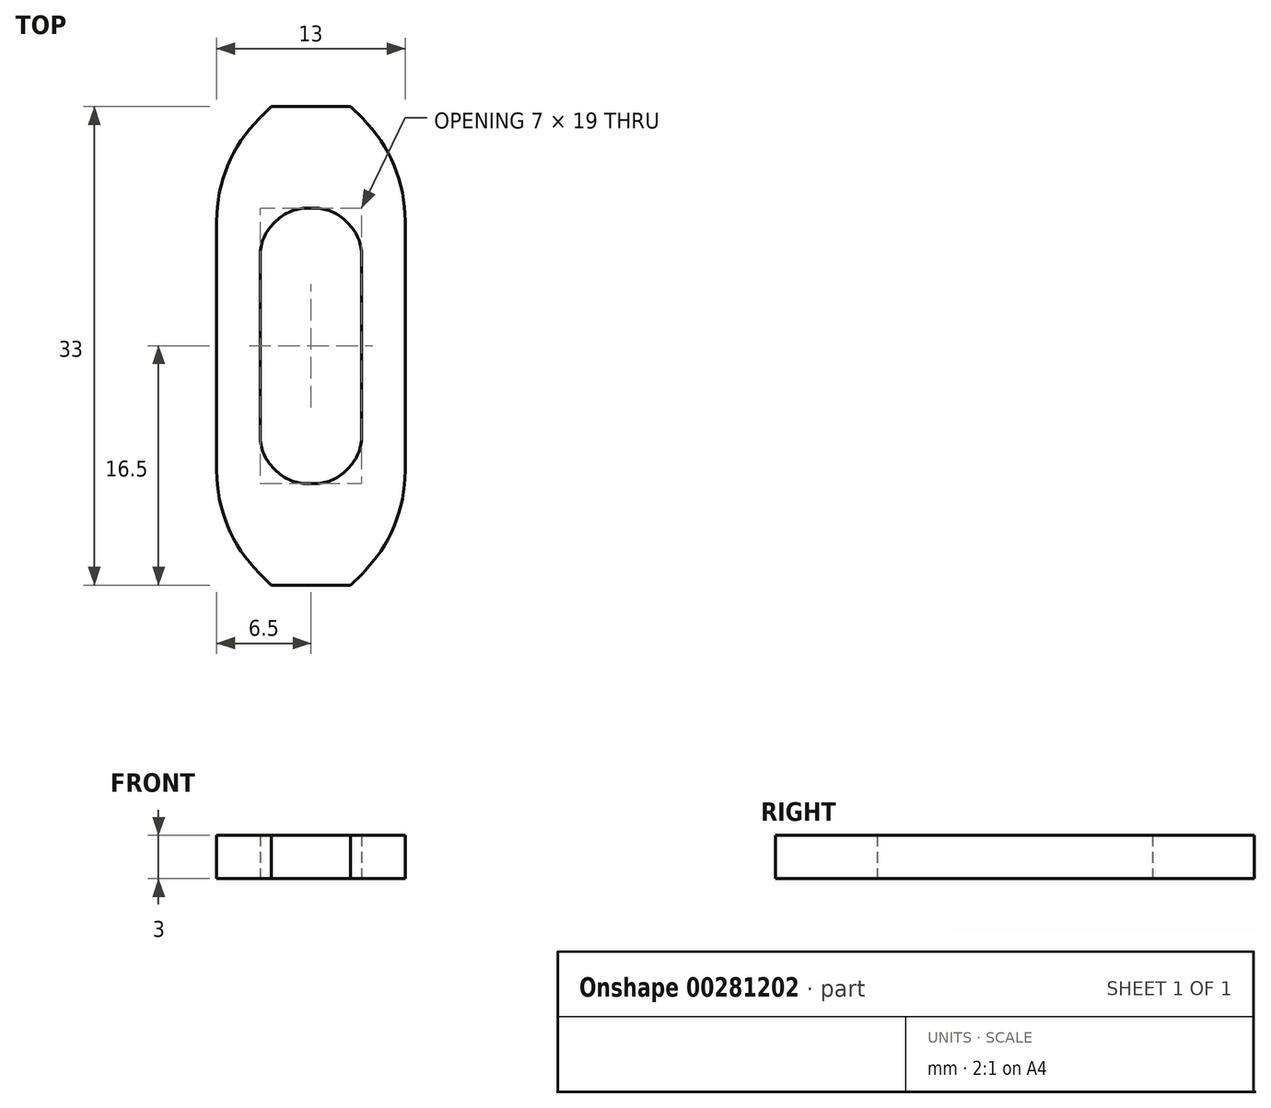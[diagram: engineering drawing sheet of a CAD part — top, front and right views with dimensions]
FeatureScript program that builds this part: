
annotation { "Feature Type Name" : "Feature", "Feature Type Description" : "" }
export const myFeature = defineFeature(function(context is Context, id is Id, definition is map)
    precondition{}
    {
        {
            var Q0;
            Q0=qCreatedBy(makeId("Top.planeOp"),FACE);
            var sketch = newSketch(context, id + "F0", { "sketchPlane" : qUnion([Q0])});
            skLineSegment(sketch, "E0.bottom", {"start": v(-1.5, 9.5) * mm, "end": v(1.5, 9.5) * mm});
            skLineSegment(sketch, "E0.top", {"start": v(-1.5, -9.5) * mm, "end": v(1.5, -9.5) * mm});
            skLineSegment(sketch, "E0.left", {"start": v(-3.5, 7.5) * mm, "end": v(-3.5, -7.5) * mm});
            skLineSegment(sketch, "E0.right", {"start": v(3.5, 7.5) * mm, "end": v(3.5, -7.5) * mm});
            skPoint(sketch, "E0.middle", {"position": v(0, 0) * mm});
            skLineSegment(sketch, "E1", {"start": v(-3.5, 7.5) * mm, "end": v(-1.5, 9.5) * mm});
            skLineSegment(sketch, "E2", {"start": v(-3.5, 0) * mm, "end": v(3.5, 0) * mm, "construction": true});
            skLineSegment(sketch, "E3", {"start": v(0, 9.5) * mm, "end": v(0, -9.5) * mm, "construction": true});
            skLineSegment(sketch, "E4.MirrorCS", {"start": v(3.5, 7.5) * mm, "end": v(1.5, 9.5) * mm});
            skLineSegment(sketch, "E5.MirrorCS", {"start": v(-3.5, -7.5) * mm, "end": v(-1.5, -9.5) * mm});
            skLineSegment(sketch, "E6.MirrorCS", {"start": v(3.5, -7.5) * mm, "end": v(1.5, -9.5) * mm});
            skPoint(sketch, "E7.orphan", {"position": v(3.5, 9.5) * mm});
            skPoint(sketch, "E8.orphan", {"position": v(3.5, -9.5) * mm});
            skPoint(sketch, "E9.orphan", {"position": v(-3.5, -9.5) * mm});
            skPoint(sketch, "E10.orphan", {"position": v(-3.5, 9.5) * mm});
            skLineSegment(sketch, "E11.0", {"start": v(-6.5, 8.74) * mm, "end": v(-2.74, 12.5) * mm, "construction": true});
            skLineSegment(sketch, "E11.1", {"start": v(-6.5, 8.74) * mm, "end": v(-6.5, -8.74) * mm});
            skLineSegment(sketch, "E11.2", {"start": v(-2.74, 12.5) * mm, "end": v(2.74, 12.5) * mm, "construction": true});
            skLineSegment(sketch, "E11.3", {"start": v(-6.5, -8.74) * mm, "end": v(-2.74, -12.5) * mm, "construction": true});
            skLineSegment(sketch, "E11.4", {"start": v(6.5, 8.74) * mm, "end": v(2.74, 12.5) * mm, "construction": true});
            skLineSegment(sketch, "E11.5", {"start": v(6.5, 8.74) * mm, "end": v(6.5, -8.74) * mm});
            skLineSegment(sketch, "E11.6", {"start": v(6.5, -8.74) * mm, "end": v(2.74, -12.5) * mm, "construction": true});
            skLineSegment(sketch, "E11.7", {"start": v(-2.74, -12.5) * mm, "end": v(2.74, -12.5) * mm});
            skLineSegment(sketch, "E12", {"start": v(-6.5, 8.74) * mm, "end": v(-6.5, 12.74) * mm});
            skLineSegment(sketch, "E13", {"start": v(-6.5, 12.74) * mm, "end": v(-2.74, 16.5) * mm});
            skLineSegment(sketch, "E14", {"start": v(-2.74, 16.5) * mm, "end": v(0, 16.5) * mm});
            skLineSegment(sketch, "E15.MirrorCS", {"start": v(2.74, 16.5) * mm, "end": v(0, 16.5) * mm});
            skLineSegment(sketch, "E16.MirrorCS", {"start": v(6.5, 12.74) * mm, "end": v(2.74, 16.5) * mm});
            skLineSegment(sketch, "E17.MirrorCS", {"start": v(6.5, 8.74) * mm, "end": v(6.5, 12.74) * mm});
            skLineSegment(sketch, "E18.MirrorCS", {"start": v(6.5, -8.74) * mm, "end": v(6.5, -12.74) * mm});
            skLineSegment(sketch, "E19.MirrorCS", {"start": v(6.5, -12.74) * mm, "end": v(2.74, -16.5) * mm});
            skLineSegment(sketch, "E20.MirrorCS", {"start": v(2.74, -16.5) * mm, "end": v(0, -16.5) * mm});
            skLineSegment(sketch, "E21.MirrorCS", {"start": v(-2.74, -16.5) * mm, "end": v(0, -16.5) * mm});
            skLineSegment(sketch, "E22.MirrorCS", {"start": v(-6.5, -12.74) * mm, "end": v(-2.74, -16.5) * mm});
            skLineSegment(sketch, "E23.MirrorCS", {"start": v(-6.5, -8.74) * mm, "end": v(-6.5, -12.74) * mm});
            skLineSegment(sketch, "E24.MirrorCS", {"start": v(-6.5, -8.74) * mm, "end": v(-2.74, -12.5) * mm});
            skLineSegment(sketch, "E25.MirrorCS", {"start": v(-2.74, -12.5) * mm, "end": v(2.74, -12.5) * mm, "construction": true});
            skSolve(sketch);
        }
        {
            var Q0;
            Q0 = qSketchRegion(id + "F0", true);
            extrude(context, id + "F1", {"entities" : qUnion([Q0]), "depth" : 3 * mm});
        }
        {
            var Q0;
            Q0=makeQuery(id+"F1.opExtrude","SWEPT_EDGE",EDGE,{"disambiguationData":[OSD([sQuery(id+"F0.wireOp",EDGE,"E0.left"),sQuery(id+"F0.wireOp",EDGE,"E1")])]});
            var Q1;
            Q1=makeQuery(id+"F1.opExtrude","SWEPT_EDGE",EDGE,{"disambiguationData":[OSD([sQuery(id+"F0.wireOp",EDGE,"E0.right"),sQuery(id+"F0.wireOp",EDGE,"E4.MirrorCS")])]});
            var Q2;
            Q2=makeQuery(id+"F1.opExtrude","SWEPT_EDGE",EDGE,{"disambiguationData":[OSD([sQuery(id+"F0.wireOp",EDGE,"E0.right"),sQuery(id+"F0.wireOp",EDGE,"E6.MirrorCS")])]});
            var Q3;
            Q3=makeQuery(id+"F1.opExtrude","SWEPT_EDGE",EDGE,{"disambiguationData":[OSD([sQuery(id+"F0.wireOp",EDGE,"E0.left"),sQuery(id+"F0.wireOp",EDGE,"E5.MirrorCS")])]});
            var Q4;
            Q4=makeQuery(id+"F1.opExtrude","SWEPT_EDGE",EDGE,{"disambiguationData":[OSD([sQuery(id+"F0.wireOp",EDGE,"E0.bottom"),sQuery(id+"F0.wireOp",EDGE,"E1")])]});
            var Q5;
            Q5=makeQuery(id+"F1.opExtrude","SWEPT_EDGE",EDGE,{"disambiguationData":[OSD([sQuery(id+"F0.wireOp",EDGE,"E0.bottom"),sQuery(id+"F0.wireOp",EDGE,"E4.MirrorCS")])]});
            var Q6;
            Q6=makeQuery(id+"F1.opExtrude","SWEPT_EDGE",EDGE,{"disambiguationData":[OSD([sQuery(id+"F0.wireOp",EDGE,"E0.top"),sQuery(id+"F0.wireOp",EDGE,"E6.MirrorCS")])]});
            var Q7;
            Q7=makeQuery(id+"F1.opExtrude","SWEPT_EDGE",EDGE,{"disambiguationData":[OSD([sQuery(id+"F0.wireOp",EDGE,"E0.top"),sQuery(id+"F0.wireOp",EDGE,"E5.MirrorCS")])]});
            fillet(context, id + "F2", {"entities" : qUnion([Q0, Q1, Q2, Q3, Q4, Q5, Q6, Q7]), "radius" : 3 * mm, "tangentPropagation" : true, "allowEdgeOverflow" : false});
        }
        {
            var Q0;
            Q0=makeQuery(id+"F1.opExtrude","SWEPT_EDGE",EDGE,{"disambiguationData":[OSD([sQuery(id+"F0.wireOp",EDGE,"E12"),sQuery(id+"F0.wireOp",EDGE,"E13")])]});
            var Q1;
            Q1=makeQuery(id+"F1.opExtrude","SWEPT_EDGE",EDGE,{"disambiguationData":[OSD([sQuery(id+"F0.wireOp",EDGE,"E16.MirrorCS"),sQuery(id+"F0.wireOp",EDGE,"E17.MirrorCS")])]});
            var Q2;
            Q2=makeQuery(id+"F1.opExtrude","SWEPT_EDGE",EDGE,{"disambiguationData":[OSD([sQuery(id+"F0.wireOp",EDGE,"E18.MirrorCS"),sQuery(id+"F0.wireOp",EDGE,"E19.MirrorCS")])]});
            var Q3;
            Q3=makeQuery(id+"F1.opExtrude","SWEPT_EDGE",EDGE,{"disambiguationData":[OSD([sQuery(id+"F0.wireOp",EDGE,"E22.MirrorCS"),sQuery(id+"F0.wireOp",EDGE,"E23.MirrorCS")])]});
            fillet(context, id + "F3", {"entities" : qUnion([Q0, Q1, Q2, Q3]), "radius" : 10 * mm, "tangentPropagation" : true, "allowEdgeOverflow" : false});
        }
    });
